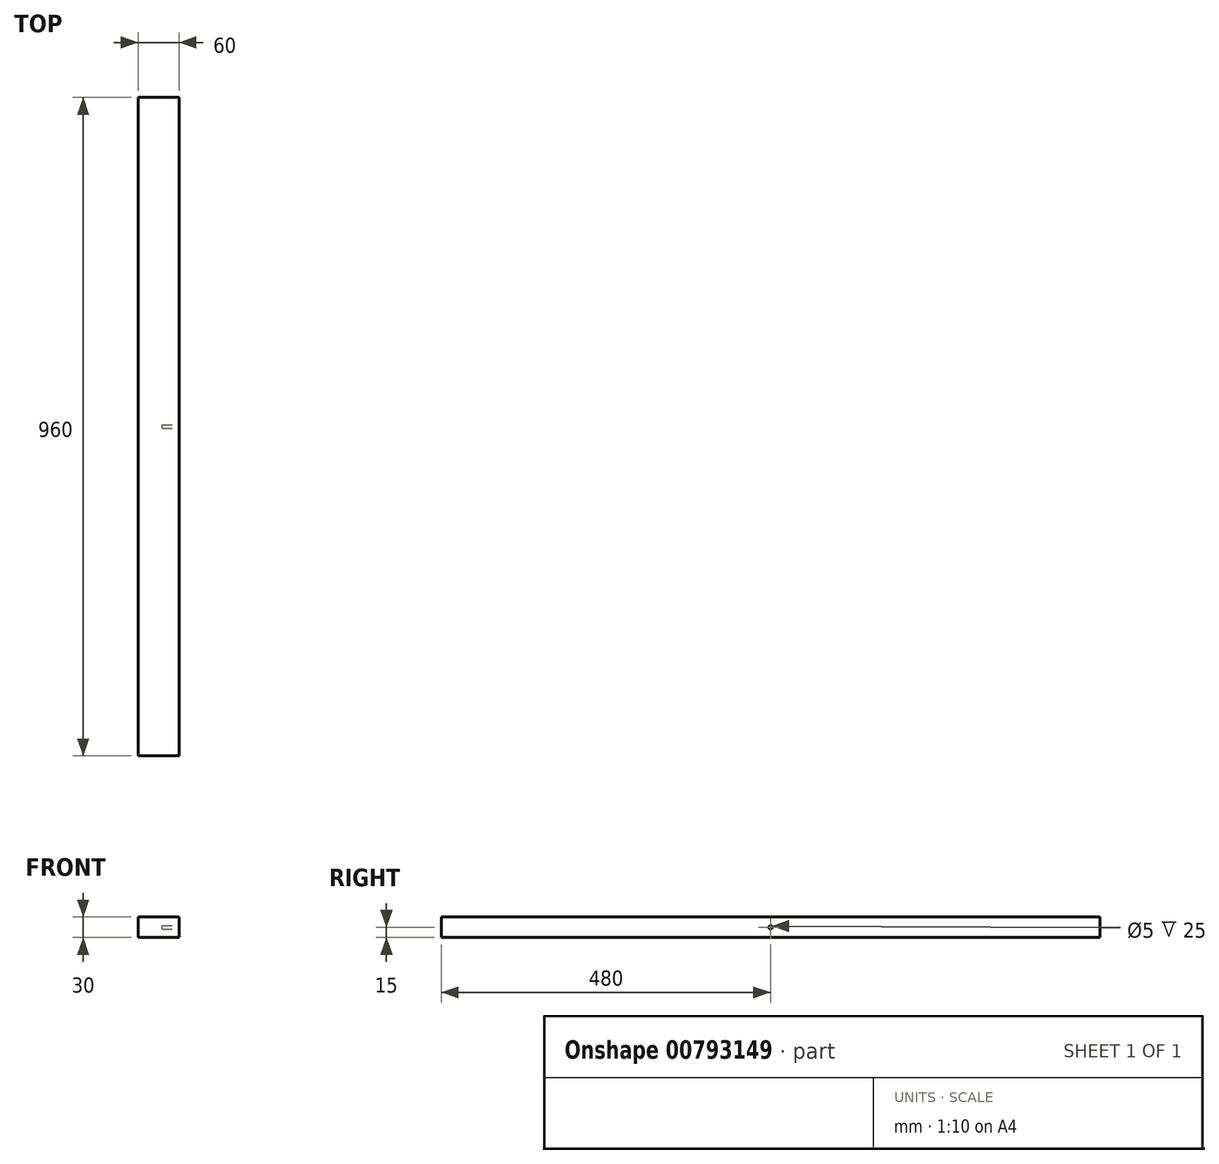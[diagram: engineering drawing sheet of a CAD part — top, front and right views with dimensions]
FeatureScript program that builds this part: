
annotation { "Feature Type Name" : "Feature", "Feature Type Description" : "" }
export const myFeature = defineFeature(function(context is Context, id is Id, definition is map)
    precondition{}
    {
        {
            var Q0;
            Q0=qCreatedBy(makeId("Front.planeOp"),FACE);
            var sketch = newSketch(context, id + "F0", { "sketchPlane" : qUnion([Q0])});
            skLineSegment(sketch, "E0.bottom", {"start": v(30, -15) * mm, "end": v(-30, -15) * mm});
            skLineSegment(sketch, "E0.top", {"start": v(30, 15) * mm, "end": v(-30, 15) * mm});
            skLineSegment(sketch, "E0.left", {"start": v(30, -15) * mm, "end": v(30, 15) * mm});
            skLineSegment(sketch, "E0.right", {"start": v(-30, -15) * mm, "end": v(-30, 15) * mm});
            skPoint(sketch, "E0.middle", {"position": v(0, 0) * mm});
            skSolve(sketch);
        }
        {
            var Q0;
            Q0=makeQuery(id+"F0.imprint","IMPRINT",FACE,{"disambiguationData":[TD([[makeQuery(id+"F0.imprint","IMPRINT",EDGE,{"derivedFrom":sQuery(id+"F0.wireOp",EDGE,"E0.bottom")}),-1.0]])]});
            extrude(context, id + "F1", {"entities" : qUnion([Q0]), "depth" : 960 * mm, "offsetDistance" : 25 * mm});
        }
        {
            var Q0;
            Q0=makeQuery(id+"F1.opExtrude","SWEPT_FACE",FACE,{"disambiguationData":[OSD([sQuery(id+"F0.wireOp",EDGE,"E0.left")])]});
            var sketch = newSketch(context, id + "F2", { "sketchPlane" : qUnion([Q0])});
            skCircle(sketch, "E1", {"center": v(-480, 0) * mm, "radius": 2.5 * mm});
            skPoint(sketch, "E1.centerSnap0", {"position": v(-480, -15) * mm});
            skSolve(sketch);
        }
        {
            var Q0;
            Q0 = qSketchRegion(id + "F2", true);
            extrude(context, id + "F3", {"entities" : qUnion([Q0]), "operationType" : NewBodyOperationType.REMOVE, "oppositeDirection" : true, "depth" : 25 * mm, "offsetDistance" : 25 * mm});
        }
    });
